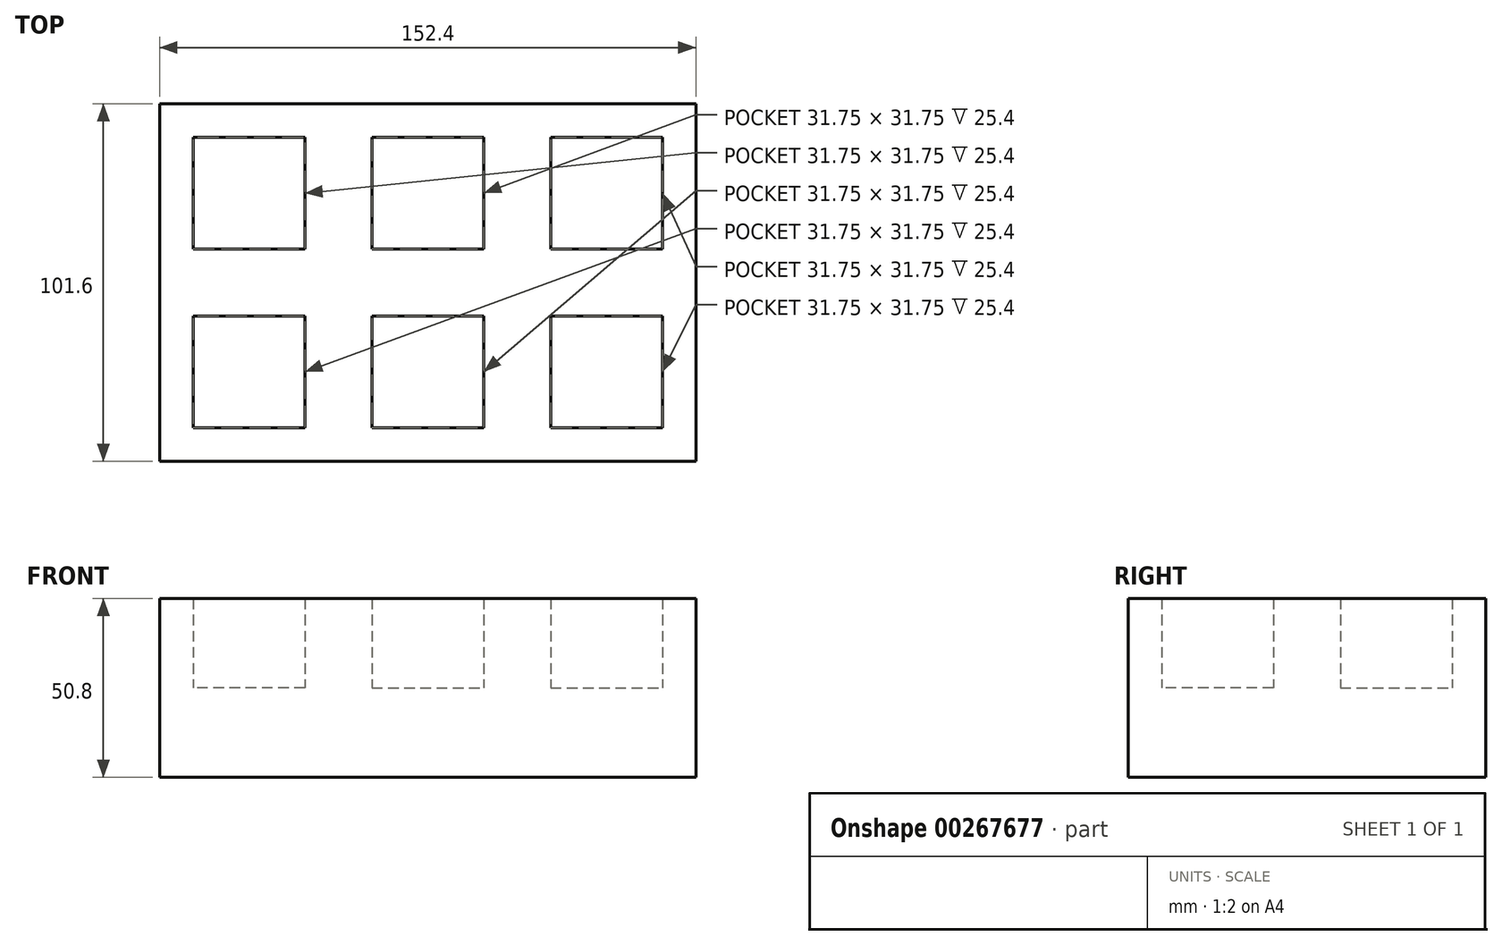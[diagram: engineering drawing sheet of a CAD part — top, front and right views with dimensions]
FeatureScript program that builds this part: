
annotation { "Feature Type Name" : "Feature", "Feature Type Description" : "" }
export const myFeature = defineFeature(function(context is Context, id is Id, definition is map)
    precondition{}
    {
        {
            var Q0;
            Q0=qCreatedBy(makeId("Top.planeOp"),FACE);
            var sketch = newSketch(context, id + "F0", { "sketchPlane" : qUnion([Q0])});
            skLineSegment(sketch, "E0.bottom", {"start": v(-15.87, 41.27) * mm, "end": v(15.88, 41.27) * mm});
            skLineSegment(sketch, "E0.top", {"start": v(-15.88, 9.53) * mm, "end": v(15.88, 9.53) * mm});
            skLineSegment(sketch, "E0.left", {"start": v(-15.87, 41.27) * mm, "end": v(-15.88, 9.53) * mm});
            skLineSegment(sketch, "E0.right", {"start": v(15.88, 41.27) * mm, "end": v(15.88, 9.53) * mm});
            skPoint(sketch, "E0.middle", {"position": v(0, 25.4) * mm});
            skLineSegment(sketch, "E1.bottom", {"start": v(-34.92, 9.52) * mm, "end": v(-66.67, 9.52) * mm});
            skLineSegment(sketch, "E1.top", {"start": v(-34.92, 41.27) * mm, "end": v(-66.67, 41.27) * mm});
            skLineSegment(sketch, "E1.left", {"start": v(-34.92, 9.52) * mm, "end": v(-34.92, 41.28) * mm});
            skLineSegment(sketch, "E1.right", {"start": v(-66.67, 9.52) * mm, "end": v(-66.67, 41.27) * mm});
            skLineSegment(sketch, "E2", {"start": v(0, 25.4) * mm, "end": v(0, 0) * mm});
            skLineSegment(sketch, "E3", {"start": v(0, 0) * mm, "end": v(0, -25.4) * mm});
            skLineSegment(sketch, "E4.bottom", {"start": v(-15.87, -9.53) * mm, "end": v(15.88, -9.53) * mm});
            skLineSegment(sketch, "E4.top", {"start": v(-15.87, -41.27) * mm, "end": v(15.88, -41.27) * mm});
            skLineSegment(sketch, "E4.left", {"start": v(-15.87, -9.53) * mm, "end": v(-15.87, -41.27) * mm});
            skLineSegment(sketch, "E4.right", {"start": v(15.88, -9.53) * mm, "end": v(15.88, -41.27) * mm});
            skPoint(sketch, "E4.middle", {"position": v(0, -25.4) * mm});
            skLineSegment(sketch, "E5.bottom", {"start": v(-34.92, -9.53) * mm, "end": v(-66.67, -9.53) * mm});
            skLineSegment(sketch, "E5.top", {"start": v(-34.92, -41.28) * mm, "end": v(-66.67, -41.28) * mm});
            skLineSegment(sketch, "E5.left", {"start": v(-34.92, -9.53) * mm, "end": v(-34.92, -41.28) * mm});
            skLineSegment(sketch, "E5.right", {"start": v(-66.67, -9.53) * mm, "end": v(-66.67, -41.28) * mm});
            skLineSegment(sketch, "E6.bottom", {"start": v(34.92, 9.53) * mm, "end": v(66.68, 9.53) * mm});
            skLineSegment(sketch, "E6.top", {"start": v(34.92, 41.27) * mm, "end": v(66.67, 41.27) * mm});
            skLineSegment(sketch, "E6.left", {"start": v(34.92, 9.53) * mm, "end": v(34.92, 41.27) * mm});
            skLineSegment(sketch, "E6.right", {"start": v(66.68, 9.53) * mm, "end": v(66.68, 41.27) * mm});
            skLineSegment(sketch, "E7.bottom", {"start": v(34.93, -9.53) * mm, "end": v(66.68, -9.53) * mm});
            skLineSegment(sketch, "E7.top", {"start": v(34.93, -41.27) * mm, "end": v(66.68, -41.27) * mm});
            skLineSegment(sketch, "E7.left", {"start": v(34.93, -9.53) * mm, "end": v(34.93, -41.27) * mm});
            skLineSegment(sketch, "E7.right", {"start": v(66.68, -9.52) * mm, "end": v(66.68, -41.27) * mm});
            skLineSegment(sketch, "E8.bottom", {"start": v(76.2, 50.8) * mm, "end": v(-76.2, 50.8) * mm});
            skLineSegment(sketch, "E8.top", {"start": v(76.2, -50.8) * mm, "end": v(-76.2, -50.8) * mm});
            skLineSegment(sketch, "E8.left", {"start": v(76.2, 50.8) * mm, "end": v(76.2, -50.8) * mm});
            skLineSegment(sketch, "E8.right", {"start": v(-76.2, 50.8) * mm, "end": v(-76.2, -50.8) * mm});
            skPoint(sketch, "E8.middle", {"position": v(0, 0) * mm});
            skSolve(sketch);
        }
        {
            var Q0;
            Q0=makeQuery(id+"F0.imprint","IMPRINT",FACE,{"disambiguationData":[TD([[makeQuery(id+"F0.imprint","IMPRINT",EDGE,{"derivedFrom":sQuery(id+"F0.wireOp",EDGE,"E0.bottom")}),1.0]])]});
            extrude(context, id + "F1", {"entities" : qUnion([Q0]), "depth" : 50.8 * mm});
        }
        {
            var Q0;
            Q0=makeQuery(id+"F0.imprint","IMPRINT",FACE,{"disambiguationData":[TD([[makeQuery(id+"F0.imprint","IMPRINT",EDGE,{"derivedFrom":sQuery(id+"F0.wireOp",EDGE,"E1.bottom")}),-1.0]])]});
            var Q1;
            Q1=makeQuery(id+"F0.imprint","IMPRINT",FACE,{"disambiguationData":[TD([[makeQuery(id+"F0.imprint","IMPRINT",EDGE,{"derivedFrom":sQuery(id+"F0.wireOp",EDGE,"E0.bottom")}),-1.0]])]});
            var Q2;
            Q2=makeQuery(id+"F0.imprint","IMPRINT",FACE,{"disambiguationData":[TD([[makeQuery(id+"F0.imprint","IMPRINT",EDGE,{"derivedFrom":sQuery(id+"F0.wireOp",EDGE,"E6.bottom")}),1.0]])]});
            var Q3;
            Q3=makeQuery(id+"F0.imprint","IMPRINT",FACE,{"disambiguationData":[TD([[makeQuery(id+"F0.imprint","IMPRINT",EDGE,{"derivedFrom":sQuery(id+"F0.wireOp",EDGE,"E7.bottom")}),-1.0]])]});
            var Q4;
            Q4=makeQuery(id+"F0.imprint","IMPRINT",FACE,{"disambiguationData":[TD([[makeQuery(id+"F0.imprint","IMPRINT",EDGE,{"derivedFrom":sQuery(id+"F0.wireOp",EDGE,"E4.top")}),1.0]])]});
            var Q5;
            Q5=makeQuery(id+"F0.imprint","IMPRINT",FACE,{"disambiguationData":[TD([[makeQuery(id+"F0.imprint","IMPRINT",EDGE,{"derivedFrom":sQuery(id+"F0.wireOp",EDGE,"E5.bottom")}),1.0]])]});
            extrude(context, id + "F2", {"entities" : qUnion([Q0, Q1, Q2, Q3, Q4, Q5]), "operationType" : NewBodyOperationType.ADD, "depth" : 25.4 * mm});
        }
    });
